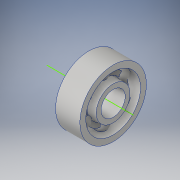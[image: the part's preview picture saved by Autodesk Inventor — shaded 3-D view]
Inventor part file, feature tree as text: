
AUTODESK INVENTOR PART (.ipt)
format: ipt  version: 2018 (Build 220112000, 112)  size: 445,440 bytes
history: native  units: in
note: dims shown in document units (in); Inventor stores cm internally (conversion verified against a paired STEP export)
features: sketch x6, revolve x5, pattern_circular x4, boolean_combine x1
ambient origin geometry x8: Origin, YZ Plane, XZ Plane, XY Plane, X Axis, Y Axis, Z Axis, Center Point
bodies: Solid1 (feature_tree), Solid2 (feature_tree)
feature tree (16):
  revolve  "Revolution1"  [1 undecoded]
  revolve  "Revolution2"  [1 undecoded]
  sketch  "Sketch3"  dims[d4=0.028in]
  pattern_circular  "Circular Pattern1"  [2 undecoded]
  revolve  "Revolution3"  [1 undecoded]
  pattern_circular  "Circular Pattern2"  Angle=90.0deg  [1 undecoded]
  revolve  "Revolution4"  Angle=360.0deg
  pattern_circular  "Circular Pattern3"  [2 undecoded]
  revolve  "Revolution5"  Angle=45.0deg
  pattern_circular  "Circular Pattern4"  [2 undecoded]
  boolean_combine  "Combine2"
  sketch  "Sketch1"  dims[d0=0.0575in d1=0.116in]
  sketch  "Sketch2"  dims[d2=0.023in d3=0.05in]
  sketch  "Sketch4"  dims[d5=90.0deg]
  sketch  "Sketch5"  dims[d6=0.058in]
  sketch  "Sketch6"  dims[d7=0.05in d8=0.025in d9=0.048in d10=90.0deg d11=2.3622in d12=360.0deg d14=0.005in d15=45.0deg d16=0.0054in d17=90.0deg d18=2.3622in d19=360.0deg d21=0.1374in d22=2.3622in d23=360.0deg d25=90.0deg d26=2.3622in d27=360.0deg]
note: 10 required parameter values undecoded (feature->parameter linkage not recoverable at this tier; creation-order binding heuristic only, values carry confidence <= 0.55)